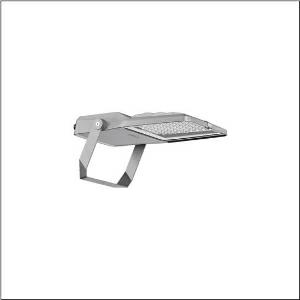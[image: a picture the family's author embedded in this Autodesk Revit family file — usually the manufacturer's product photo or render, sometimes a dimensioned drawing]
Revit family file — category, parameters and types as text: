
# Revit family: floodlight_fl_21_iq_mini___pl61_5xa7771b2c1a_d515
name_source: partatom
category: Lighting Fixtures
units: mm (PartAtom-declared; Revit-internal decimal feet)

## family parameters
Cut with Voids When Loaded = No
Host = Face
Light Source = No
Part Type = Normal
Room Calculation Point = No
Round Connector Dimension = Use Diameter
Shared = No

## types (1)
- --- (1 x LED, 6120 lm, 45.5 W, 3000K)
    Apparent Load = 46 VA
    CIE Flux Codes = 33 65 98 100 100
    Color Rendering = 70
    Color Temperature = 3000K
    Default Elevation = 1800 mm
    Description = Floodlight FL 21 iQ mini, floodlight, primary light control with lens, of PMMA, primary optical cover: protective disc, of toughened safety glass, transparent, light distribution: PL61, light emission: direct distribution, installation type: surface-mounted, LED, High Power LED, rated luminous flux: 6.120lm, luminous efficacy: 135lm/W, light colour: 730, colour temperature: 3000K, control gear: iQ Comfort/DALI, control: Auto-Match, Temp-Guard, Lumen-Switch, Night-Set, Smart-Wire, Light-Fading, Desk-Remote (wireless, voltage-free reading and setting of iQ features in the workshop via application-optimized NFC function/RFID function), optimised constant luminous flux control (CLO 2.0), with terminal, 6-pole, mains connection: 220..240V, AC, 50/60Hz, start of lifetime: 46W, end of service life: 48W, reduction: 22W, luminaire housing, of diecast aluminium, powder-coated, Siteco® metallic grey (DB 702S), corrosivity category C5 mid according to DIN EN ISO 12944, suitable for swimming pools, chlorine-resistant, sealing non-destructively replaceable, mounting bracket, of steel, galvanised, powder-coated, Siteco® metallic grey (DB 702S), protection rating (complete): IP66, insulation class (complete): insulation class II (safety insulation), certification: CE, ENEC, VDE, protection symbol: D, impact resistance: IK08, permissible operating ambient temperature: -40..+40°C, permissible operating ambient temperature for outdoor applications: -40..+50°C, standard: DIN EN 12944, LABS conformity tested according to VDMA 24364:2018-05, packaging unit: 1 piece

Light Distribution: PL61
    Height = 70 mm
    Lamp = 1 x LED
    Lamp Light Flux = 6120 lm
    Lamp Power = 45.5 W
    Lamp count = 1
    Length = 485 mm
    Luminous efficacy = 135 lm/W
    Manufacturer = Siteco
    ModVariant = No
    Model = 5XA7771B2C1A
    Mounting Place = Wall
    Mounting Type = Surface mounted
    Number of Poles = 1
    OnlyDefault = Yes
    Power Factor = 1
    Product Name = Floodlight FL 21 iQ mini | PL61
    Product group = floodlight | wall mounted
    ProductGroupID = 2001
    Protection Class = Protection class II
    Protection Degree = IP 66
    RLX_Detail_Level = 1
    RLX_Emergency_Light_Flux = 0 lm
    RLX_Emergency_Type = 0
    RLX_Emergency_Type_DB = No
    RlxData = <blob elided: 96337 chars, md5=8634ec95>
    Socket = socket
    Standby Power = 0 W
    System Light Flux = 6120 lm
    System Power = 46 W
    Type Comments = factory setting: luminous flux: 100 % | dim-lin: 254 | 463 mA
    Type Image = l_1006845.jpg
    URL = http://relux.com
    VarID = @adj_173908
    Voltage = 0 V
    Weight = 0.00 kg
    Width = 337 mm

## geometry (parser evidence)
native form markers: Blend x4, Sweep x11
no freeform markers — native parametric forms only
